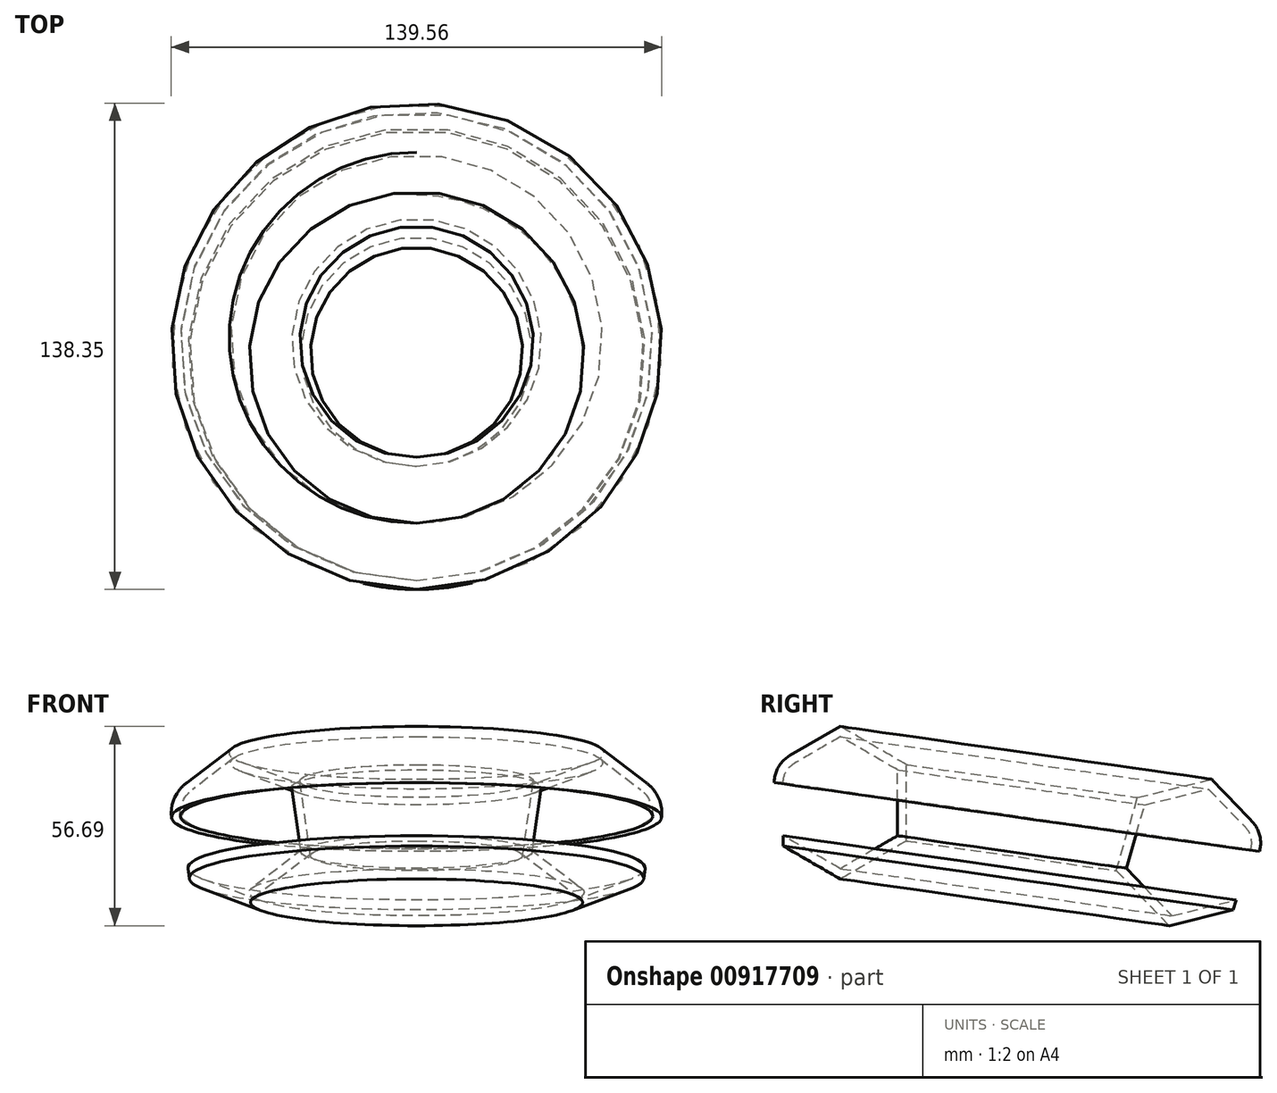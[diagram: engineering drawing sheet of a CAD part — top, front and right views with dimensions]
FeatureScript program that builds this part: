
annotation { "Feature Type Name" : "Feature", "Feature Type Description" : "" }
export const myFeature = defineFeature(function(context is Context, id is Id, definition is map)
    precondition{}
    {
        {
            var Q0;
            Q0=qCreatedBy(makeId("Right.planeOp"),FACE);
            var sketch = newSketch(context, id + "F0", { "sketchPlane" : qUnion([Q0])});
            skCircle(sketch, "E0.cCircle", {"center": v(-16.25, 9.34) * mm, "radius": 16.25 * mm, "construction": true});
            skLineSegment(sketch, "E0.0", {"start": v(0, 18.72) * mm, "end": v(0, -0.04) * mm});
            skLineSegment(sketch, "E0.1", {"start": v(0, -0.04) * mm, "end": v(-16.25, -9.43) * mm});
            skLineSegment(sketch, "E0.2", {"start": v(-16.25, -9.43) * mm, "end": v(-32.5, -0.04) * mm});
            skLineSegment(sketch, "E0.3", {"start": v(-32.5, -0.04) * mm, "end": v(-32.5, 15.06) * mm});
            skLineSegment(sketch, "E0.4", {"start": v(-29.33, 20.56) * mm, "end": v(-16.25, 28.1) * mm});
            skLineSegment(sketch, "E0.5", {"start": v(-16.25, 28.1) * mm, "end": v(0, 18.72) * mm});
            skPoint(sketch, "E0.0.midPoint", {"position": v(0, 9.34) * mm});
            skPoint(sketch, "E1.visualSharp", {"position": v(-32.5, 18.72) * mm});
            skArc(sketch, "E1.filletArc", {"start": v(-29.33, 20.56) * mm, "mid": v(-31.65, 18.23) * mm, "end": v(-32.5, 15.06) * mm});
            skLineSegment(sketch, "E2", {"start": v(39.64, 45.23) * mm, "end": v(28.02, -36.55) * mm, "construction": true});
            skSolve(sketch);
        }
        {
            var Q0;
            Q0 = qSketchRegion(id + "F0", true);
            var Q1;
            Q1=sQuery(id+"F0.wireOp",EDGE,"E2");
            revolve(context, id + "F1", {"surfaceOperationType" : NewSurfaceOperationType.NEW, "entities" : qUnion([Q0]), "axis" : qUnion([Q1]), "revolveType" : RevolveType.FULL});
        }
        {
            var Q0;
            Q0=makeQuery(id+"F1.opRevolve","SWEPT_FACE",FACE,{"disambiguationData":[OSD([sQuery(id+"F0.wireOp",EDGE,"E0.3")])]});
            var Q1;
            Q1=makeQuery(id+"F1.opRevolve","SWEPT_BODY",BODY,{"disambiguationData":[OSD([sQuery(id+"F0.wireOp",EDGE,"E0.0"),sQuery(id+"F0.wireOp",EDGE,"E0.1"),sQuery(id+"F0.wireOp",EDGE,"E0.2"),sQuery(id+"F0.wireOp",EDGE,"E0.3"),sQuery(id+"F0.wireOp",EDGE,"E0.4"),sQuery(id+"F0.wireOp",EDGE,"E0.5"),sQuery(id+"F0.wireOp",EDGE,"E1.filletArc")])]});
            shell(context, id + "F2", {"entities" : qUnion([Q0]), "parts" : qUnion([Q1]), "thickness" : 2.54 * mm, "oppositeDirection" : true});
        }
    });
